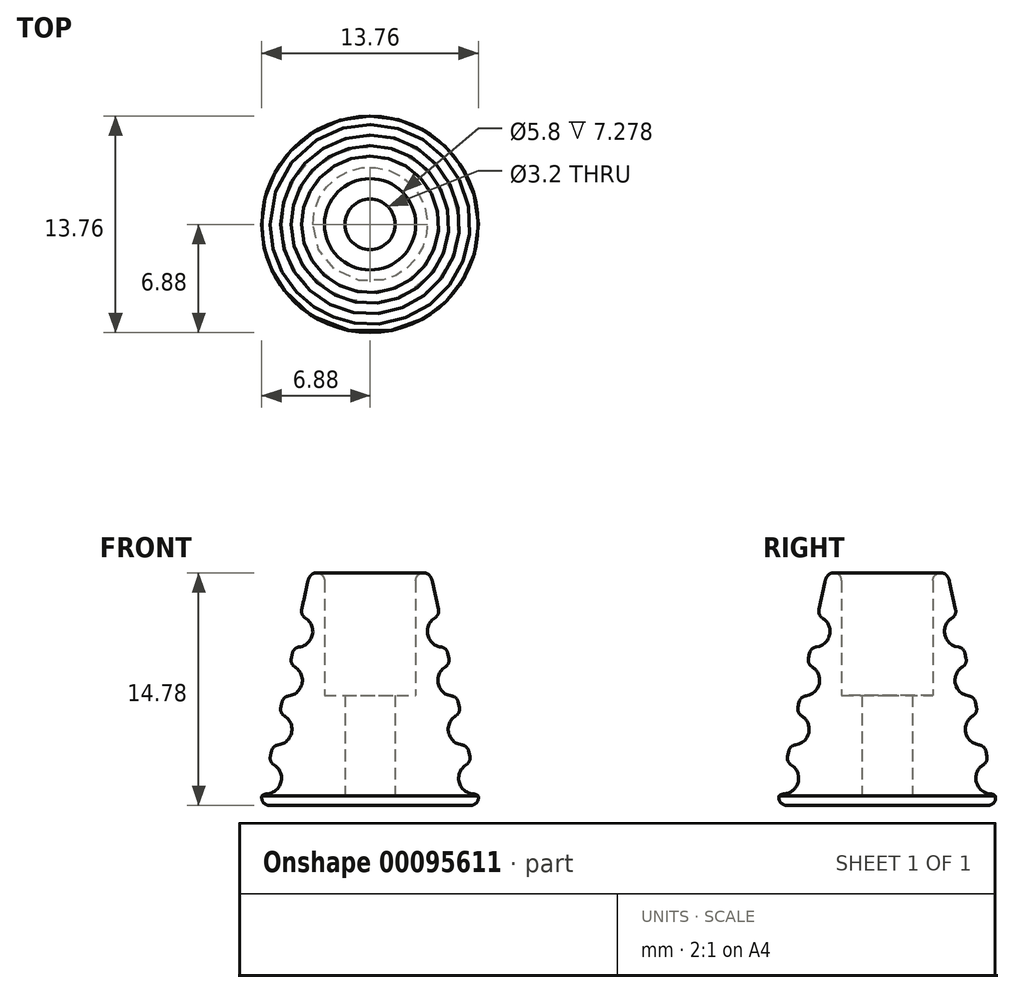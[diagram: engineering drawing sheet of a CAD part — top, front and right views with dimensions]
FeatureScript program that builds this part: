
annotation { "Feature Type Name" : "Feature", "Feature Type Description" : "" }
export const myFeature = defineFeature(function(context is Context, id is Id, definition is map)
    precondition{}
    {
        {
            var Q0;
            Q0=qCreatedBy(makeId("Right.planeOp"),FACE);
            var sketch = newSketch(context, id + "F0", { "sketchPlane" : qUnion([Q0])});
            skLineSegment(sketch, "E0", {"start": v(1.6, 0) * mm, "end": v(7, 0) * mm});
            skLineSegment(sketch, "E1", {"start": v(7, 0) * mm, "end": v(6.84, 0.75) * mm});
            skLineSegment(sketch, "E2", {"start": v(3.8, 15) * mm, "end": v(2.9, 15) * mm});
            skLineSegment(sketch, "E3", {"start": v(2.9, 15) * mm, "end": v(2.9, 7) * mm});
            skLineSegment(sketch, "E4", {"start": v(2.9, 7) * mm, "end": v(1.6, 7) * mm});
            skLineSegment(sketch, "E5", {"start": v(1.6, 7) * mm, "end": v(1.6, 0) * mm});
            skLineSegment(sketch, "E6", {"start": v(0, 0) * mm, "end": v(0, 8.5) * mm, "construction": true});
            skArc(sketch, "E7", {"start": v(4.43, 12.03) * mm, "mid": v(3.66, 10.85) * mm, "end": v(4.85, 10.08) * mm});
            skArc(sketch, "E8.1.0.0", {"start": v(5.1, 8.93) * mm, "mid": v(4.32, 7.74) * mm, "end": v(5.51, 6.97) * mm});
            skArc(sketch, "E8.2.0.0", {"start": v(5.76, 5.82) * mm, "mid": v(4.98, 4.63) * mm, "end": v(6.17, 3.86) * mm});
            skArc(sketch, "E8.3.0.0", {"start": v(6.42, 2.7) * mm, "mid": v(5.65, 1.52) * mm, "end": v(6.84, 0.75) * mm});
            skLineSegment(sketch, "E8.direction1", {"start": v(4.84, 10.08) * mm, "end": v(5.3, 7.95) * mm, "construction": true});
            skLineSegment(sketch, "E9.trimOffspring", {"start": v(4.43, 12.03) * mm, "end": v(3.8, 15) * mm});
            skLineSegment(sketch, "E10.trimOffspring", {"start": v(5.1, 8.93) * mm, "end": v(4.85, 10.08) * mm});
            skLineSegment(sketch, "E11.trimOffspring", {"start": v(5.76, 5.82) * mm, "end": v(5.51, 6.97) * mm});
            skLineSegment(sketch, "E12.trimOffspring", {"start": v(6.42, 2.7) * mm, "end": v(6.17, 3.86) * mm});
            skSolve(sketch);
        }
        {
            var Q0;
            Q0 = qSketchRegion(id + "F0", true);
            var Q1;
            Q1=sQuery(id+"F0.wireOp",EDGE,"E6");
            revolve(context, id + "F1", {"entities" : qUnion([Q0]), "axis" : qUnion([Q1]), "revolveType" : RevolveType.FULL});
        }
        {
            var Q0;
            Q0=makeQuery(id+"F1.opRevolve","SWEPT_EDGE",EDGE,{"disambiguationData":[OSD([sQuery(id+"F0.wireOp",EDGE,"E0"),sQuery(id+"F0.wireOp",EDGE,"E1")])]});
            fillet(context, id + "F2", {"entities" : qUnion([Q0]), "radius" : .5 * mm, "tangentPropagation" : true, "allowEdgeOverflow" : false});
        }
        {
            var Q0;
            Q0=makeQuery(id+"F1.opRevolve","SWEPT_EDGE",EDGE,{"disambiguationData":[OSD([sQuery(id+"F0.wireOp",EDGE,"E2"),sQuery(id+"F0.wireOp",EDGE,"E9.trimOffspring")])]});
            fillet(context, id + "F3", {"entities" : qUnion([Q0]), "radius" : 1 * mm, "tangentPropagation" : true, "allowEdgeOverflow" : false});
        }
        {
            var Q0;
            Q0=makeQuery(id+"F1.opRevolve","SWEPT_EDGE",EDGE,{"disambiguationData":[OSD([sQuery(id+"F0.wireOp",EDGE,"E2"),sQuery(id+"F0.wireOp",EDGE,"E3")])]});
            fillet(context, id + "F4", {"entities" : qUnion([Q0]), "radius" : .5 * mm, "tangentPropagation" : true, "allowEdgeOverflow" : false});
        }
        {
            var Q0;
            Q0=makeQuery(id+"F1.opRevolve","SWEPT_EDGE",EDGE,{"disambiguationData":[OSD([sQuery(id+"F0.wireOp",EDGE,"E8.3.0.0"),sQuery(id+"F0.wireOp",EDGE,"E12.trimOffspring")])]});
            var Q1;
            Q1=makeQuery(id+"F1.opRevolve","SWEPT_EDGE",EDGE,{"disambiguationData":[OSD([sQuery(id+"F0.wireOp",EDGE,"E8.2.0.0"),sQuery(id+"F0.wireOp",EDGE,"E12.trimOffspring")])]});
            var Q2;
            Q2=makeQuery(id+"F1.opRevolve","SWEPT_EDGE",EDGE,{"disambiguationData":[OSD([sQuery(id+"F0.wireOp",EDGE,"E8.2.0.0"),sQuery(id+"F0.wireOp",EDGE,"E11.trimOffspring")])]});
            var Q3;
            Q3=makeQuery(id+"F1.opRevolve","SWEPT_EDGE",EDGE,{"disambiguationData":[OSD([sQuery(id+"F0.wireOp",EDGE,"E8.1.0.0"),sQuery(id+"F0.wireOp",EDGE,"E11.trimOffspring")])]});
            var Q4;
            Q4=makeQuery(id+"F1.opRevolve","SWEPT_EDGE",EDGE,{"disambiguationData":[OSD([sQuery(id+"F0.wireOp",EDGE,"E8.1.0.0"),sQuery(id+"F0.wireOp",EDGE,"E10.trimOffspring")])]});
            var Q5;
            Q5=makeQuery(id+"F1.opRevolve","SWEPT_EDGE",EDGE,{"disambiguationData":[OSD([sQuery(id+"F0.wireOp",EDGE,"E7"),sQuery(id+"F0.wireOp",EDGE,"E10.trimOffspring")])]});
            var Q6;
            Q6=makeQuery(id+"F1.opRevolve","SWEPT_EDGE",EDGE,{"disambiguationData":[OSD([sQuery(id+"F0.wireOp",EDGE,"E7"),sQuery(id+"F0.wireOp",EDGE,"E9.trimOffspring")])]});
            var Q7;
            Q7=makeQuery(id+"F1.opRevolve","SWEPT_EDGE",EDGE,{"disambiguationData":[OSD([sQuery(id+"F0.wireOp",EDGE,"E1"),sQuery(id+"F0.wireOp",EDGE,"E8.3.0.0")])]});
            fillet(context, id + "F5", {"entities" : qUnion([Q0, Q1, Q2, Q3, Q4, Q5, Q6, Q7]), "radius" : .5 * mm, "tangentPropagation" : true, "allowEdgeOverflow" : false});
        }
    });
